# Revit family: FU_Inspec_Archal_2-5-MB
name_source: partatom
category: Furniture
units: mm (PartAtom-declared; Revit-internal decimal feet)

## family parameters
Always vertical = Yes
Cut with Voids When Loaded = No
OmniClass Number = 23.40.20.00
OmniClass Title = General Furniture and Specialties
Room Calculation Point = No
Shared = No
Work Plane-Based = No

## types (2) — shared parameters
Armrest Material = Metal - Chrome - Polished
Assembly Code = E2020
Castor Material = Plastic - Black
Frame Material = Metal - Chrome - Polished
Keynote = 46.B
Manufacturer = Inspec
Not Quilted = No
Quilted = Yes
URL = https://inspecfurniture.com
zero-valued in all types: Default Elevation

## per-type parameters (varying)
| type | Description | Model | Seat Material |
| Archal 1.5MB - Chrome - Beige | Fully upholstered chair with medium height back on a powder coated or chromium plated steel base, upholstery with quilting detail. | Archal 1.5 MB | Fabric - Divina Beige |
| Archal 2.5MB - Chrome- Brown | Fully Upholstered Chair with medium height back, upholstery with quilting detail. | Archal 2.5 MB | Leather - Rustical - Dark brown |

## geometry (parser evidence)
native form markers: Blend x7
no freeform markers — native parametric forms only
